# Revit family: SYSIMPLE FDT54A
name_source: partatom
category: Оборудование
units: mm (PartAtom-declared; Revit-internal decimal feet)

## family parameters
Всегда вертикально = Да
На основе рабочей плоскости = Нет
Общий = Нет
При загрузке вырезать с полостями = Нет
Размер круглого соединителя = Использовать диаметр
Тип детали = Нормальный
Точка расчета площади = Нет

## types (1)
- SYSIMPLE FDT54A
    Air guide size(mm) = /
    Body dimension(mm) = 1129×518×240
    COP = /
    Capacity = /
    Chassis height（mm) = /
    Compressor quantity = /
    Compressor type = /
    Cooling Power input = /
    Cooling capacity = 5400/4595/3514
    Cooling current = /
    Current of Circuit breaker = /
    Drain Pipe (mm) = Rc 3/4"
    EER = /
    Front clearance(mm) = /
    Heating capacity = 8100/6898/5275
    Heating current = /
    Heating power input = /
    Hydraulic Resistance = 40
    Inlet/Outlet Water Pipe (mm) = Rc 3/4"
    Installation hole spacing（D) = /
    Installation hole spacing（W) = /
    Left Side clearance(ODU side mm) = /
    Left Side clearance(wall side mm) = /
    Manufacturer = AUX
    Manufacturer URL = /
    Max.Current input = /
    Max.Power input = /
    Max.Working pressure = 1.6
    Model = AFC-600HCR/4BA6
    Noise Level(dB) = ≤47
    Operation range Heatling (°C） = /
    Operation range cooling (°C） = /
    Power = 220~240V,50Hz,1
    Product series = FCU-Horizontal duct 6 series 50HZ
    Protection grade = /
    Rear clearance(mm) = /
    Right Side clearance(ODU side mm) = /
    Right Side clearance(wall side mm) = /
    Static pressure（pa） = 30
    Water Flow Volume = 1.08
    Weight(G) = 23.7
    Weight(N) = 20.2
    fan type = Low noise 3-speed fan motor ( PG40A )
